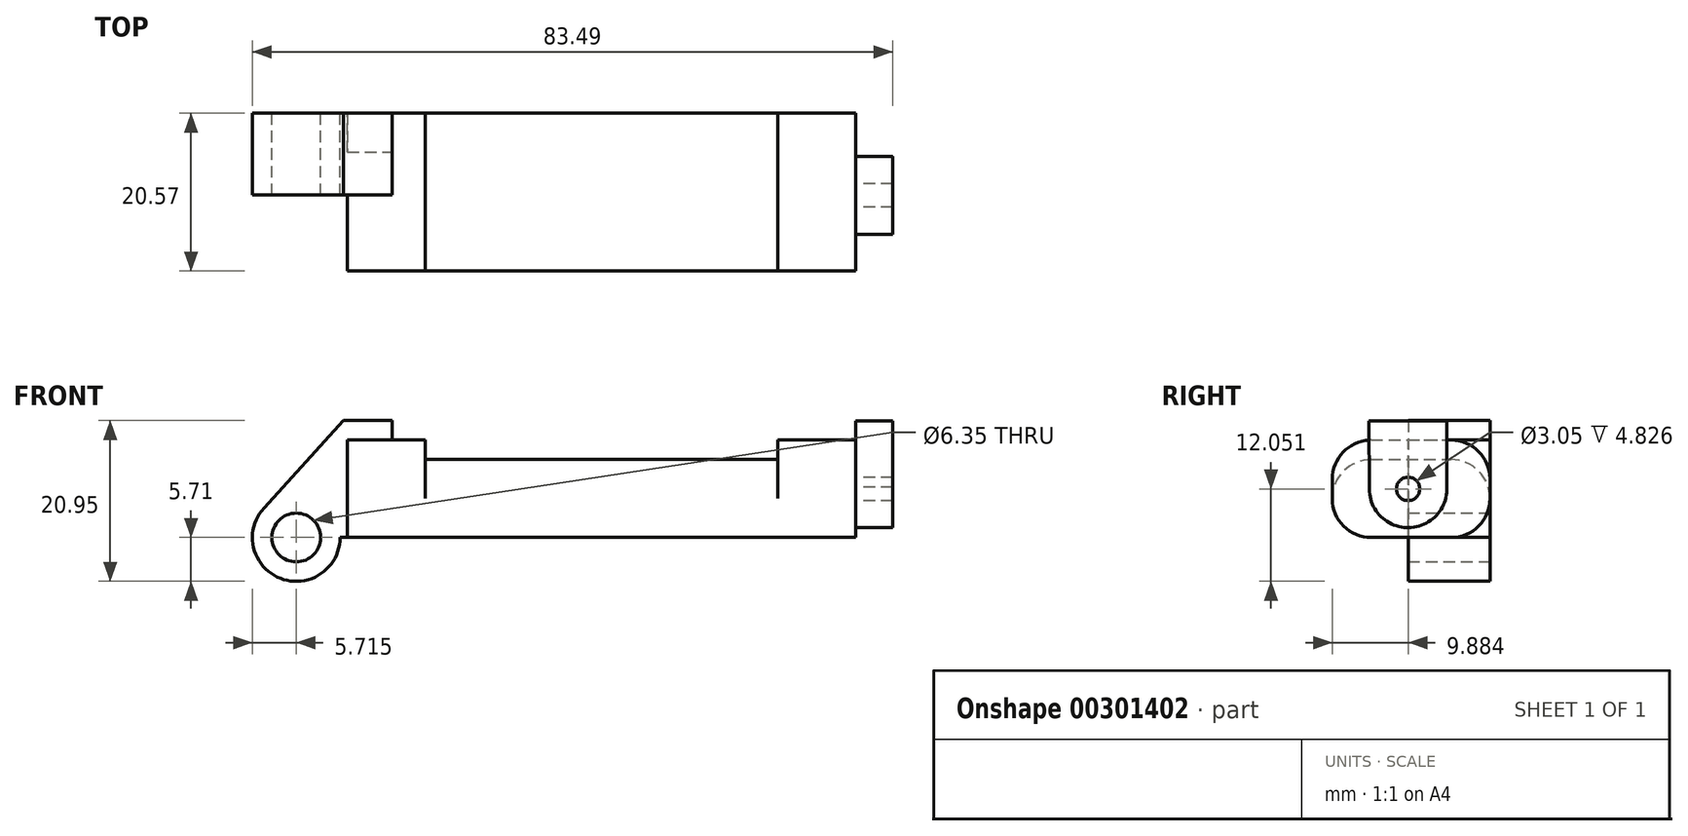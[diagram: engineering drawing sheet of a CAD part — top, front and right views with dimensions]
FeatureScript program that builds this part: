
annotation { "Feature Type Name" : "Feature", "Feature Type Description" : "" }
export const myFeature = defineFeature(function(context is Context, id is Id, definition is map)
    precondition{}
    {
        {
            var Q0;
            Q0=qCreatedBy(makeId("Front.planeOp"),FACE);
            var sketch = newSketch(context, id + "F0", { "sketchPlane" : qUnion([Q0])});
            skLineSegment(sketch, "E0", {"start": v(0, 0) * mm, "end": v(0, 12.7) * mm});
            skLineSegment(sketch, "E1", {"start": v(0, 12.7) * mm, "end": v(10.16, 12.7) * mm});
            skLineSegment(sketch, "E2", {"start": v(10.16, 12.7) * mm, "end": v(10.16, 10.16) * mm});
            skLineSegment(sketch, "E3", {"start": v(10.16, 10.16) * mm, "end": v(56.13, 10.16) * mm});
            skLineSegment(sketch, "E4", {"start": v(56.13, 10.16) * mm, "end": v(56.13, 12.7) * mm});
            skLineSegment(sketch, "E5", {"start": v(56.13, 12.7) * mm, "end": v(66.3, 12.7) * mm});
            skLineSegment(sketch, "E6", {"start": v(66.3, 12.7) * mm, "end": v(66.3, 0) * mm});
            skLineSegment(sketch, "E7", {"start": v(66.3, 0) * mm, "end": v(0, 0) * mm});
            skLineSegment(sketch, "E8", {"start": v(5.84, 15.24) * mm, "end": v(-0.5, 15.24) * mm});
            skLineSegment(sketch, "E9", {"start": v(-0.5, 15.24) * mm, "end": v(-10.88, 3.85) * mm});
            skLineSegment(sketch, "E10", {"start": v(0, 0) * mm, "end": v(-6.65, 0) * mm});
            skCircle(sketch, "E11", {"center": v(-6.65, 0) * mm, "radius": 5.72 * mm});
            skCircle(sketch, "E12", {"center": v(-6.65, 0) * mm, "radius": 3.18 * mm});
            skLineSegment(sketch, "E13", {"start": v(5.84, 15.24) * mm, "end": v(5.84, -9.4) * mm});
            skLineSegment(sketch, "E14", {"start": v(5.84, -9.4) * mm, "end": v(-8.18, -5.5) * mm});
            skSolve(sketch);
        }
        {
            var Q0;
            {var subQ0=sQuery(id+"F0.wireOp",EDGE,"E2");Q0=makeQuery(id+"F0.imprint","IMPRINT",FACE,{"disambiguationData":[TD([[makeQuery(id+"F0.imprint","IMPRINT",EDGE,{"derivedFrom":subQ0}),-1.0]])]});}
            var Q1;
            {var subQ0=sQuery(id+"F0.wireOp",EDGE,"E0");Q1=makeQuery(id+"F0.imprint","IMPRINT",FACE,{"disambiguationData":[TD([[makeQuery(id+"F0.imprint","IMPRINT",EDGE,{"derivedFrom":subQ0}),-1.0]])]});}
            extrude(context, id + "F1", {"entities" : qUnion([Q0, Q1]), "depth" : 20.57 * mm});
        }
        {
            var Q0;
            Q0=makeQuery(id+"F1.opExtrude","CAP_EDGE",EDGE,{"disambiguationData":[OSD([sQuery(id+"F0.wireOp",EDGE,"E3")])],"isStart":true});
            var Q1;
            Q1=makeQuery(id+"F1.opExtrude","CAP_EDGE",EDGE,{"disambiguationData":[OSD([sQuery(id+"F0.wireOp",EDGE,"E3")])],"isStart":false});
            fillet(context, id + "F2", {"entities" : qUnion([Q0, Q1]), "radius" : 5.08 * mm, "tangentPropagation" : true, "allowEdgeOverflow" : false});
        }
        {
            var Q0;
            Q0=makeQuery(id+"F1.opExtrude","CAP_EDGE",EDGE,{"disambiguationData":[OSD([sQuery(id+"F0.wireOp",EDGE,"E7")])],"isStart":true});
            var Q1;
            Q1=makeQuery(id+"F1.opExtrude","CAP_EDGE",EDGE,{"disambiguationData":[OSD([sQuery(id+"F0.wireOp",EDGE,"E5")])],"isStart":true});
            var Q2;
            Q2=makeQuery(id+"F1.opExtrude","CAP_EDGE",EDGE,{"disambiguationData":[OSD([sQuery(id+"F0.wireOp",EDGE,"E5")])],"isStart":false});
            var Q3;
            Q3=makeQuery(id+"F1.opExtrude","CAP_EDGE",EDGE,{"disambiguationData":[OSD([sQuery(id+"F0.wireOp",EDGE,"E1")])],"isStart":true});
            var Q4;
            Q4=makeQuery(id+"F1.opExtrude","CAP_EDGE",EDGE,{"disambiguationData":[OSD([sQuery(id+"F0.wireOp",EDGE,"E1")])],"isStart":false});
            var Q5;
            Q5=makeQuery(id+"F1.opExtrude","CAP_EDGE",EDGE,{"disambiguationData":[OSD([sQuery(id+"F0.wireOp",EDGE,"E7")])],"isStart":false});
            fillet(context, id + "F3", {"entities" : qUnion([Q0, Q1, Q2, Q3, Q4, Q5]), "radius" : 5.08 * mm, "tangentPropagation" : true, "allowEdgeOverflow" : false});
        }
        {
            var Q0;
            {var subQ5=sQuery(id+"F0.wireOp",EDGE,"E12");Q0=makeQuery(id+"F0.imprint","IMPRINT",FACE,{"disambiguationData":[TD([[makeQuery(id+"F0.imprint","IMPRINT",EDGE,{"derivedFrom":subQ5}),-1.0]])]});}
            var Q1;
            {var subQ1=sQuery(id+"F0.wireOp",EDGE,"E0");Q1=makeQuery(id+"F0.imprint","IMPRINT",FACE,{"disambiguationData":[TD([[makeQuery(id+"F0.imprint","IMPRINT",EDGE,{"derivedFrom":subQ1}),1.0]])]});}
            extrude(context, id + "F4", {"entities" : qUnion([Q0, Q1]), "operationType" : NewBodyOperationType.ADD, "depth" : 10.67 * mm});
        }
        {
            var Q0;
            Q0=makeQuery(id+"F1.opExtrude","SWEPT_FACE",FACE,{"disambiguationData":[OSD([sQuery(id+"F0.wireOp",EDGE,"E6")])]});
            var sketch = newSketch(context, id + "F5", { "sketchPlane" : qUnion([Q0])});
            skCircle(sketch, "E15", {"center": v(-10.69, 6.34) * mm, "radius": 5.06 * mm});
            skCircle(sketch, "E16", {"center": v(-10.69, 6.34) * mm, "radius": 1.53 * mm});
            skLineSegment(sketch, "E17", {"start": v(-5.63, 6.54) * mm, "end": v(-5.63, 15.23) * mm});
            skLineSegment(sketch, "E18", {"start": v(-5.63, 15.23) * mm, "end": v(-14.78, 15.23) * mm});
            skLineSegment(sketch, "E19", {"start": v(-14.78, 15.23) * mm, "end": v(-15.78, 15.23) * mm});
            skLineSegment(sketch, "E20", {"start": v(-15.78, 15.23) * mm, "end": v(-15.74, 6.32) * mm});
            skSolve(sketch);
        }
        {
            var Q0;
            {var subQ8=sQuery(id+"F5.wireOp",EDGE,"E18");Q0=makeQuery(id+"F5.imprint","IMPRINT",FACE,{"disambiguationData":[TD([[makeQuery(id+"F5.imprint","IMPRINT",EDGE,{"derivedFrom":subQ8}),1.0]])]});}
            var Q1;
            {var subQ5=sQuery(id+"F5.wireOp",EDGE,"E17");var subQ8=sQuery(id+"F5.wireOp",EDGE,"E15");var subQ11=makeQuery(id+"F5.imprint","INTERSECT",VERTEX,{"derivedFrom":[subQ8,subQ5]});Q1=makeQuery(id+"F5.imprint","IMPRINT",FACE,{"disambiguationData":[TD([[makeQuery(id+"F5.imprint","IMPRINT",EDGE,{"disambiguationData":[TD([[subQ11,-1.0]])],"derivedFrom":subQ8}),-1.0]])]});}
            var Q2;
            Q2=makeQuery(id+"F5.imprint","IMPRINT",FACE,{"disambiguationData":[TD([[makeQuery(id+"F5.imprint","IMPRINT",EDGE,{"derivedFrom":sQuery(id+"F5.wireOp",EDGE,"E16")}),-1.0]])]});
            extrude(context, id + "F6", {"entities" : qUnion([Q0, Q1, Q2]), "operationType" : NewBodyOperationType.ADD, "depth" : 4.83 * mm});
        }
    });
